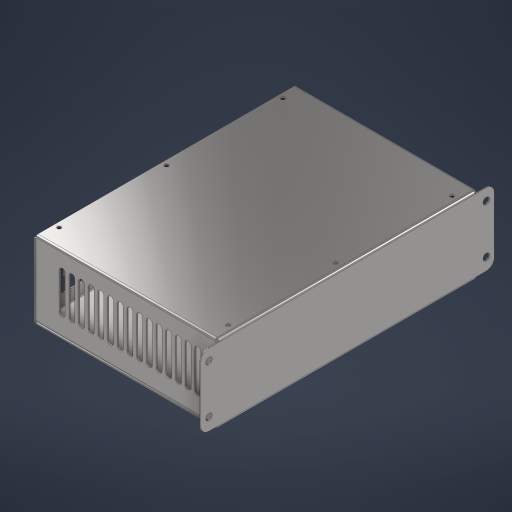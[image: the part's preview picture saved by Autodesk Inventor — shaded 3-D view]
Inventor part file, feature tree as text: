
AUTODESK INVENTOR PART (.ipt)
format: ipt  version: 2024.2 (Build 282272000, 272)  size: 967,168 bytes
history: native  units: in
note: dims shown in document units (in); Inventor stores cm internally (conversion verified against a paired STEP export)
features: sketch x33, sheet_metal_op x20, hole x20, other x14, chamfer x8, plane x5, mirror x1, pattern_linear x1
ambient origin geometry x8: Origin, YZ Plane, XZ Plane, XY Plane, X Axis, Y Axis, Z Axis, Center Point
bodies: Solid1 (feature_tree), Solid2 (feature_tree)
feature tree (102):
  sketch  "Sketch1"  dims[d0=0.063in d1=0.3125in]
  plane  "Work Plane1"
  sketch  "Sketch2"  dims[d4=0.1in d5=0.25in]
  sheet_metal_op  "Contour Flange1"
  sheet_metal_op  "Contour Flange2"
  sheet_metal_op  "Flange1"
  plane  "Work Plane5"
  sketch  "Sketch5"  dims[d10=7.8898in d13=0.0815in]
  plane  "Work Plane6"
  sketch  "Sketch6"  dims[d14=0.1115in d15=8.0013in]
  sheet_metal_op  "Contour Flange3"
  chamfer  "Corner Round1"
  sheet_metal_op  "Flange2"
  sheet_metal_op  "Flange3"
  chamfer  "Corner Round2"
  plane  "Work Plane7"
  mirror  "Mirror1"
  sketch  "Sketch11"  dims[d24=0.126in d25=0.0315in]
  sketch  "Sketch Driven Pattern1"  dims[d2=5.4409in d3=0.17in]
  chamfer  "Corner Round3"
  chamfer  "Corner Round4"
  plane  "Work Plane8"
  sketch  "Sketch13"  dims[d28=0.0157in]
  chamfer  "Corner Round5"
  hole  "Hole1"  [1 undecoded]
  hole  "Hole2"  [1 undecoded]
  hole  "Hole3"  [1 undecoded]
  hole  "Hole4"  [1 undecoded]
  hole  "Hole5"  [1 undecoded]
  hole  "Hole6"  [1 undecoded]
  hole  "Hole7"  [1 undecoded]
  hole  "Hole8"  [1 undecoded]
  hole  "Hole9"  [1 undecoded]
  hole  "Hole10"  [1 undecoded]
  hole  "Hole11"  [1 undecoded]
  hole  "Hole12"  [1 undecoded]
  hole  "Hole13"  [1 undecoded]
  pattern_linear  "Rectangular Pattern1"  Spacing1=0.35in  [1 undecoded]
  sketch  "Sketch28"  dims[d45=0.126in]
  sketch  "Sketch29"  dims[d46=0.0315in]
  sketch  "Sketch30"  dims[d47=0.0315in]
  sheet_metal_op  "Face1"
  chamfer  "Corner Round6"
  hole  "Hole14"  [1 undecoded]
  hole  "Hole15"  [1 undecoded]
  hole  "Hole16"  [1 undecoded]
  hole  "Hole17"  [1 undecoded]
  hole  "Hole18"  [1 undecoded]
  hole  "Hole19"  [1 undecoded]
  hole  "Hole20"  [1 undecoded]
  chamfer  "Corner Round8"
  chamfer  "Corner Round9"
  other  "Plate1"
  sheet_metal_op  "Bend1"
  sheet_metal_op  "Corner1"
  other  "Plate2"
  sheet_metal_op  "Bend2"
  sheet_metal_op  "Corner2"
  sketch  "Sketch3"  dims[d6=1.63in d7=0.04in]
  other  "Plate3"
  sheet_metal_op  "Bend3"
  sheet_metal_op  "Corner3"
  sketch  "Sketch4"  dims[d8=0.375in d9=0.1in]
  other  "Plate4"
  sheet_metal_op  "Bend4"
  sheet_metal_op  "Corner4"
  sketch  "Sketch7"  dims[d16=0.0315in d17=0.0315in]
  sketch  "Sketch8"  dims[d18=0.0157in d19=0.063in]
  other  "Plate5"
  sheet_metal_op  "Bend5"
  sheet_metal_op  "Corner5"
  sketch  "Sketch9"  dims[d20=0.0315in d21=8.0013in]
  other  "Plate6"
  sheet_metal_op  "Bend6"
  sheet_metal_op  "Corner6"
  sketch  "Sketch10"  dims[d22=0.0315in d23=0.031in]
  sketch  "Sketch12"  dims[d26=0.0315in d27=0.0315in]
  sketch  "Sketch14"  dims[d29=0.063in]
  sketch  "Sketch15"  dims[d30=0.0315in]
  sketch  "Sketch16"  dims[d31=0.0815in]
  sketch  "Sketch17"  dims[d32=0.0315in]
  sketch  "Sketch18"  dims[d33=0.031in]
  sketch  "Sketch19"  dims[d34=0.126in]
  sketch  "Sketch20"  dims[d35=0.0315in]
  sketch  "Sketch21"  dims[d36=0.0315in]
  sketch  "Sketch22"  dims[d37=0.0315in]
  sketch  "Sketch23"  dims[d38=0.0157in]
  sketch  "Sketch24"  dims[d39=0.063in]
  sketch  "Sketch25"  dims[d40=0.0315in]
  sketch  "Sketch26"  dims[d41=0.375in d42=90.0deg d43=0.0315in]
  sketch  "Sketch27"  dims[d44=0.02in]
  other  "Plate7"
  sheet_metal_op  "Bend7"
  sketch  "Sketch31"  dims[d48=0.063in]
  sketch  "Sketch33"  dims[d49=0.0in d50=0.35in d51=0.0315in d52=0.0315in d53=0.25in d54=5.545in d55=0.0315in d56=0.0315in d57=0.0157in d58=0.063in d59=0.0315in d60=5.545in d61=0.0315in d62=0.031in d63=0.126in d64=0.0315in d65=0.0315in d66=0.0945in d67=0.0in d68=0.05in d69=0.0315in d70=0.0157in d71=0.063in d72=0.0315in d73=0.5in d74=0.0in d75=0.0315in d76=0.126in d77=0.0315in d78=0.0315in d79=0.0315in d80=0.0157in d81=0.063in d82=0.0315in d83=0.5in d84=0.0in d85=0.0315in d86=0.126in d87=0.0315in d88=0.0315in d89=0.25in d90=0.2in d91=1.5in d92=0.36in d93=0.0315in d94=0.0in d95=1.2598in d96=1.5in d97=0.1457in d98=0.7in d101=1.5748in d103=360.0deg d106=0.04in d107=1.2in d108=1.2in d109=0.25in d110=1.5748in d112=360.0deg d114=2.0in d115=0.0315in d116=0.0in d117=7.8898in d118=0.063in d119=1.6969in d120=3.0945in d121=0.5709in d122=1.1417in d123=0.1378in d124=0.1378in d125=0.1378in d126=2.0079in d127=0.6693in d128=0.5138in d129=0.5512in d131=0.2559in d132=0.315in d133=0.1969in d134=0.5138in d135=0.5512in d136=0.315in d137=0.1969in d138=0.9646in d139=0.5512in d140=0.315in d141=0.1969in d142=0.4331in d143=0.4331in d144=0.1772in d145=0.2165in d146=0.5984in d147=0.4331in d148=0.1772in d149=0.2165in d150=0.1969in d151=0.689in d152=1.0236in d153=1.0138in d154=0.0394in d155=0.0197in d156=0.0197in d157=0.13in d158=0.4331in d160=0.4331in d161=0.3125in d162=0.0394in d163=0.0315in d164=0.0in d165=0.04in d166=0.03in d167=0.3in d168=1.2598in d169=2.2441in d170=2.3228in d171=1.685in d172=0.25in d173=0.3in d174=2.1799in d175=1.6535in d176=1.4961in d177=0.3in d180=0.1in d181=0.1285in d182=0.75in d183=0.375in d184=0.25in d185=0.5635in d186=1.0in d187=0.0in d188=0.1285in d189=0.75in d190=0.375in d191=0.25in d192=0.5635in d193=1.0in d194=0.0in d195=0.1285in d196=0.75in d197=0.375in d198=0.25in d199=0.5635in d200=1.0in d201=0.0in d202=0.1285in d203=0.75in d204=0.375in d205=0.25in d206=0.5635in d207=1.0in d208=0.0in d209=0.1285in d210=0.75in d211=0.375in d212=0.25in d213=0.5635in d214=1.0in d215=0.0in d216=0.1285in d217=0.75in d218=0.375in d219=0.25in d220=0.5635in d221=1.0in d222=0.0in d223=0.1285in d224=0.75in d225=0.375in d226=0.25in d227=0.5635in d228=1.0in d229=0.0in d230=0.1285in d231=0.75in d232=0.375in d233=0.25in d234=0.5635in d235=1.0in d236=0.0in d237=0.1285in d238=0.75in d239=0.375in d240=0.25in d241=0.5635in d242=1.0in d243=0.0in d244=0.1285in d245=0.75in d246=0.375in d247=0.25in d248=0.5635in d249=1.0in d250=0.0in d251=0.1285in d252=0.75in d253=0.375in d254=0.25in d255=0.5635in d256=1.0in d257=0.0in d258=0.1285in d259=0.75in d260=0.375in d261=0.25in d262=0.5635in d263=1.0in d264=0.0in d265=0.1285in d266=0.75in d267=0.375in d268=0.25in d269=0.5635in d270=1.0in d271=0.0in d272=0.18in d273=0.0315in d274=0.0in d275=5.9055in d277=0.3in d279=0.5in d281=0.5in d282=3.6in d283=3.5in d284=3.5in d285=0.116in d286=0.75in d287=0.219in d288=0.112in d289=0.5635in d290=0.0315in d291=0.8108in d292=0.116in d293=0.75in d294=0.375in d295=0.25in d296=0.5635in d297=0.0315in d298=0.8108in d299=0.116in d300=0.75in d301=0.375in d302=0.25in d303=0.5635in d304=0.0315in d305=0.8108in d306=0.166in d307=0.75in d308=0.375in d309=0.25in d310=0.5635in d311=0.063in d312=0.0in d313=0.166in d314=0.75in d315=0.375in d316=0.25in d317=0.5635in d318=0.063in d319=0.0in d320=0.166in d321=0.75in d322=0.375in d323=0.25in d324=0.5635in d325=0.063in d326=0.0in d327=0.23in d328=0.23in d329=0.0315in d330=0.0315in d331=0.0157in d332=0.063in d333=0.0315in d334=0.1in d335=1.3in d336=0.5in d337=0.25in d338=0.75in d339=0.375in d340=0.25in d341=0.5635in d342=0.0315in d343=0.0in d348=0.44in d349=0.063in d350=0.0in d351=0.12in d352=0.02in]
  other  "Cut1"
  other  "Cut2"
  other  "Cut3"
  other  "Cut4"
  other  "Cut5"
  other  "Cut7"
  other  "Cut9"
note: 21 required parameter values undecoded (feature->parameter linkage not recoverable at this tier; creation-order binding heuristic only, values carry confidence <= 0.55)
